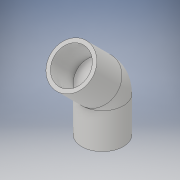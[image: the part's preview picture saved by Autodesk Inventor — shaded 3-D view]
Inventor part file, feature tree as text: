
AUTODESK INVENTOR PART (.ipt)
format: ipt  version: 2018 (Build 220112000, 112)  size: 144,896 bytes
history: native  units: in
note: dims shown in document units (in); Inventor stores cm internally (conversion verified against a paired STEP export)
features: sketch x7, plane x5, extrude x4, revolve x1
ambient origin geometry x8: Origin, YZ Plane, XZ Plane, XY Plane, X Axis, Y Axis, Z Axis, Center Point
bodies: Solid1 (feature_tree)
feature tree (17):
  extrude  "Extrusion1"  Depth=1.367in TaperAngle=0.0deg
  sketch  "Sketch2"  dims[d3=-0.3092in d4=1.367in d5=0.0in]
  plane  "Work Plane1"
  extrude  "Extrusion2"  Depth=1.367in TaperAngle=0.0deg
  extrude  "Extrusion3"  Depth=1.25in TaperAngle=0.0deg
  extrude  "Extrusion4"  Depth=1.25in TaperAngle=0.0deg
  plane  "Work Plane2"
  plane  "Work Plane3"
  revolve  "Revolution1"  [1 undecoded]
  plane  "Work Plane4"
  sketch  "Sketch6"  dims[d14=45.0deg]
  plane  "Work Plane5"
  sketch  "Sketch8"  dims[d15=-0.3092in]
  sketch  "Sketch1"  dims[d0=1.605in d1=1.367in d2=0.0in]
  sketch  "Sketch3"  dims[d6=1.321in d7=1.25in d8=0.0in]
  sketch  "Sketch4"  dims[d9=1.321in d10=1.25in d11=0.0in]
  sketch  "Sketch5"  dims[d12=0.0in d13=0.0in]
note: 1 required parameter value undecoded (feature->parameter linkage not recoverable at this tier; creation-order binding heuristic only, values carry confidence <= 0.55)
